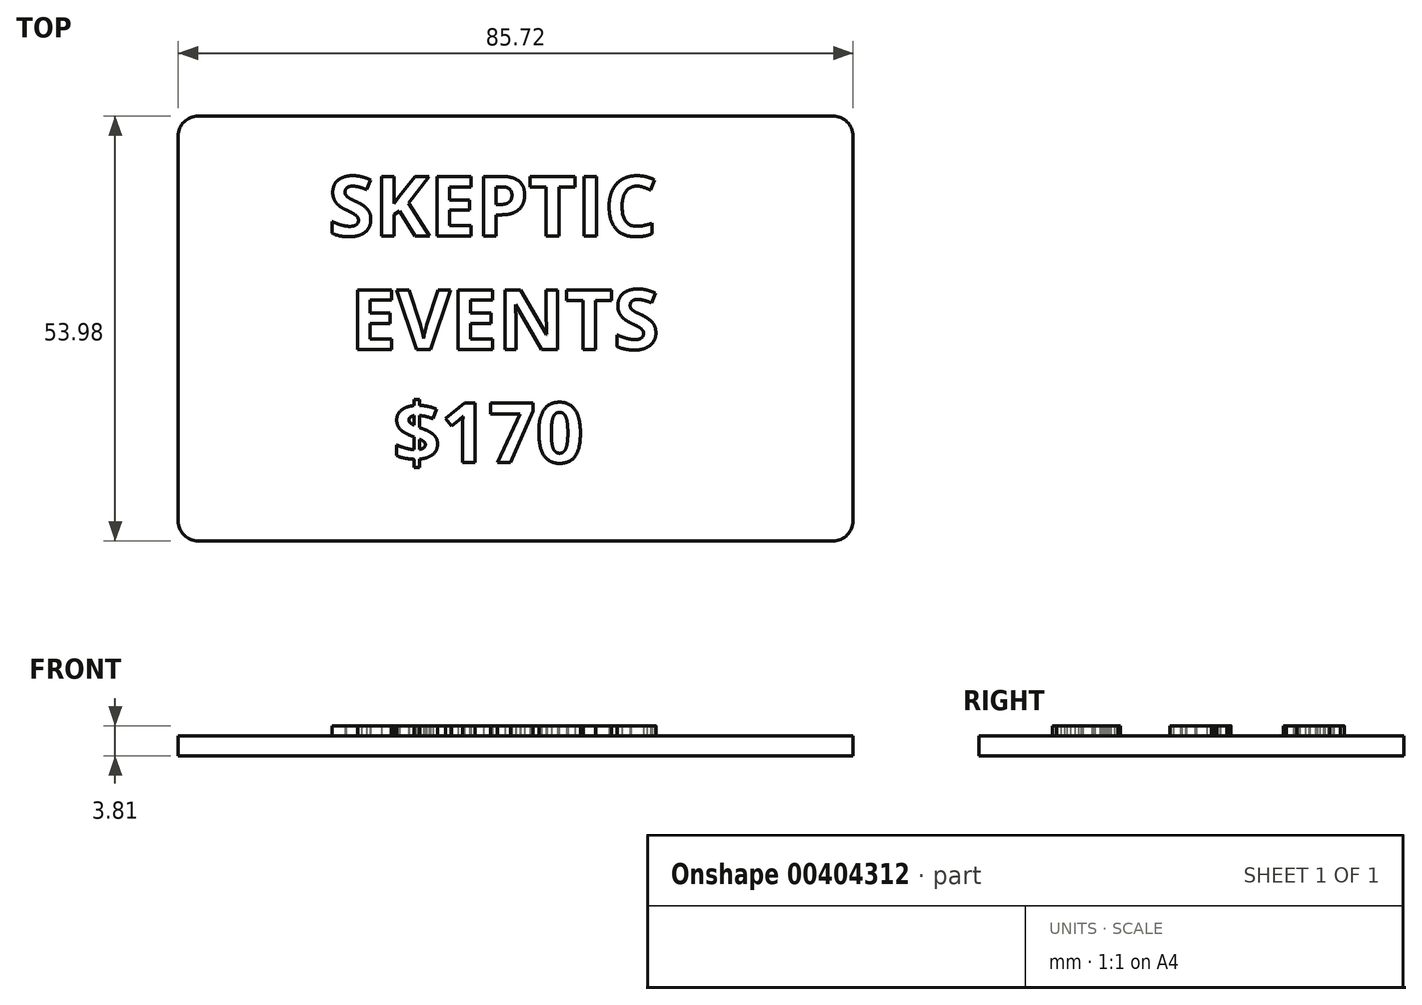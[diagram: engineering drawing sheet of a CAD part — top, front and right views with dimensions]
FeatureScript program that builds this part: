
annotation { "Feature Type Name" : "Feature", "Feature Type Description" : "" }
export const myFeature = defineFeature(function(context is Context, id is Id, definition is map)
    precondition{}
    {
        {
            var Q0;
            Q0=qCreatedBy(makeId("Top.planeOp"),FACE);
            var sketch = newSketch(context, id + "F0", { "sketchPlane" : qUnion([Q0])});
            skLineSegment(sketch, "E0.bottom", {"start": v(40.32, 26.99) * mm, "end": v(-40.32, 26.99) * mm});
            skLineSegment(sketch, "E0.top", {"start": v(40.32, -26.99) * mm, "end": v(-40.32, -26.99) * mm});
            skLineSegment(sketch, "E0.left", {"start": v(42.86, 24.45) * mm, "end": v(42.86, -24.45) * mm});
            skLineSegment(sketch, "E0.right", {"start": v(-42.86, 24.45) * mm, "end": v(-42.86, -24.45) * mm});
            skPoint(sketch, "E0.middle", {"position": v(0, 0) * mm});
            skPoint(sketch, "E1.visualSharp", {"position": v(42.86, 26.99) * mm});
            skArc(sketch, "E1.filletArc", {"start": v(42.86, 24.45) * mm, "mid": v(42.12, 26.24) * mm, "end": v(40.32, 26.99) * mm});
            skPoint(sketch, "E2.visualSharp", {"position": v(42.86, -26.99) * mm});
            skArc(sketch, "E2.filletArc", {"start": v(40.32, -26.99) * mm, "mid": v(42.12, -26.24) * mm, "end": v(42.86, -24.45) * mm});
            skPoint(sketch, "E3.visualSharp", {"position": v(-42.86, -26.99) * mm});
            skArc(sketch, "E3.filletArc", {"start": v(-42.86, -24.45) * mm, "mid": v(-42.12, -26.24) * mm, "end": v(-40.32, -26.99) * mm});
            skPoint(sketch, "E4.visualSharp", {"position": v(-42.86, 26.99) * mm});
            skArc(sketch, "E4.filletArc", {"start": v(-40.32, 26.99) * mm, "mid": v(-42.12, 26.24) * mm, "end": v(-42.86, 24.45) * mm});
            skSolve(sketch);
        }
        {
            var Q0;
            Q0=makeQuery(id+"F0.imprint","IMPRINT",FACE,{"disambiguationData":[TD([[makeQuery(id+"F0.imprint","IMPRINT",EDGE,{"derivedFrom":sQuery(id+"F0.wireOp",EDGE,"E0.bottom")}),1.0]])]});
            extrude(context, id + "F1", {"entities" : qUnion([Q0]), "depth" : 2.54 * mm});
        }
        {
            var Q0;
            Q0=makeQuery(id+"F1.opExtrude","CAP_FACE",FACE,{"disambiguationData":[OSD([sQuery(id+"F0.wireOp",EDGE,"E0.bottom"),sQuery(id+"F0.wireOp",EDGE,"E0.top"),sQuery(id+"F0.wireOp",EDGE,"E0.left"),sQuery(id+"F0.wireOp",EDGE,"E0.right"),sQuery(id+"F0.wireOp",EDGE,"E1.filletArc"),sQuery(id+"F0.wireOp",EDGE,"E2.filletArc"),sQuery(id+"F0.wireOp",EDGE,"E3.filletArc"),sQuery(id+"F0.wireOp",EDGE,"E4.filletArc")])],"isStart":false});
            var sketch = newSketch(context, id + "F2", { "sketchPlane" : qUnion([Q0])});
            skText(sketch, "E5", { "text": "SKEPTIC\n EVENTS\n   $170", "fontName": "OpenSans-Bold.ttf"});
            const initialGuessF2  = {"E5": [-0.02381, 0.01175, 1, 0, 0.00762]};
            skSetInitialGuess(sketch, initialGuessF2);
            skSolve(sketch);
        }
        {
            var Q0;
            Q0=qSketchRegion(id+"F2",true);
            extrude(context, id + "F3", {"entities" : qUnion([Q0]), "operationType" : NewBodyOperationType.ADD, "depth" : 1.27 * mm});
        }
    });
